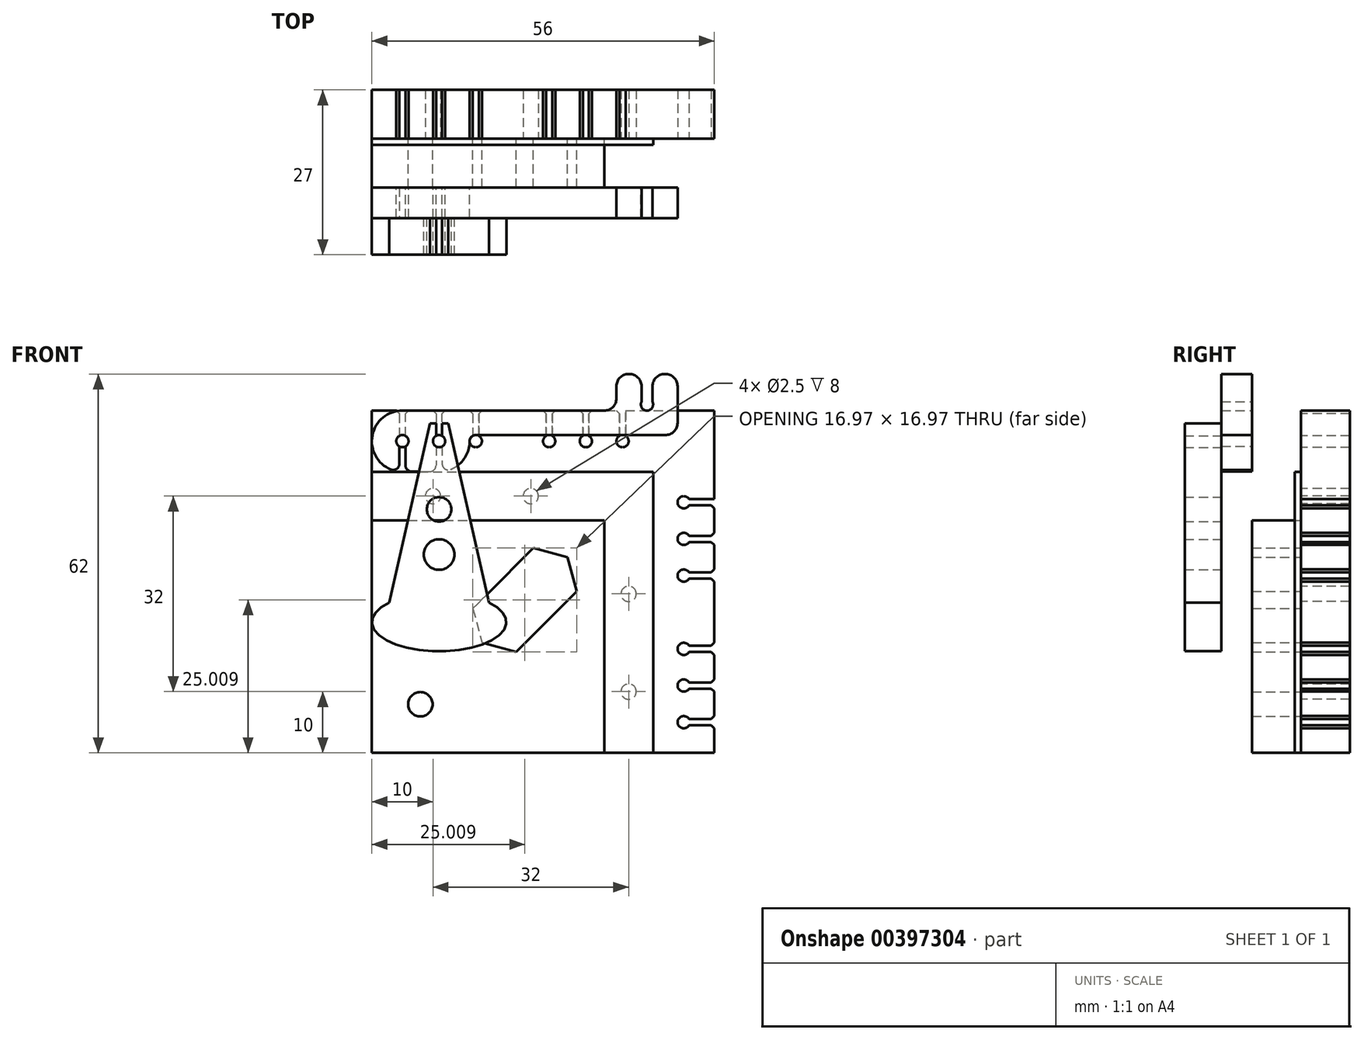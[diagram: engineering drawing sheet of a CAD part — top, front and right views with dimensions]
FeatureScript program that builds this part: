
annotation { "Feature Type Name" : "Feature", "Feature Type Description" : "" }
export const myFeature = defineFeature(function(context is Context, id is Id, definition is map)
    precondition{}
    {
        {
            assignVariable(context, id + "F0", {"name" : "Samm", "anyValue" : 4 * mm});
        }
        {
            assignVariable(context, id + "F1", {"name" : "Auk", "anyValue" : 2 * mm});
        }
        {
            assignVariable(context, id + "F2", {"name" : "Paksus", "anyValue" : getVariable(context, 'Samm') + getVariable(context, 'Auk') + getVariable(context, 'Samm') / 2});
        }
        {
            var Q0;
            Q0=qCreatedBy(makeId("Front.planeOp"),FACE);
            var sketch = newSketch(context, id + "F3", { "sketchPlane" : qUnion([Q0])});
            skLineSegment(sketch, "E0.bottom", {"start": v(0, 0) * mm, "end": v(56, 0) * mm});
            skLineSegment(sketch, "E0.top", {"start": v(0, 56) * mm, "end": v(56, 56) * mm});
            skLineSegment(sketch, "E0.left", {"start": v(0, 0) * mm, "end": v(0, 56) * mm});
            skLineSegment(sketch, "E0.right", {"start": v(56, 0) * mm, "end": v(56, 56) * mm});
            skLineSegment(sketch, "E1", {"start": v(0, 0) * mm, "end": v(56, 56) * mm});
            skLineSegment(sketch, "E2", {"start": v(0, 46) * mm, "end": v(46, 46) * mm});
            skLineSegment(sketch, "E3", {"start": v(0, 38) * mm, "end": v(38, 38) * mm});
            skLineSegment(sketch, "E4", {"start": v(0, 51) * mm, "end": v(56, 51) * mm, "construction": true});
            skLineSegment(sketch, "E5", {"start": v(46, 46) * mm, "end": v(46, 56) * mm, "construction": true});
            skLineSegment(sketch, "E6", {"start": v(38, 38) * mm, "end": v(38, 56) * mm, "construction": true});
            skLineSegment(sketch, "E7", {"start": v(0, 42) * mm, "end": v(42, 42) * mm, "construction": true});
            skPoint(sketch, "E8", {"position": v(26, 42) * mm});
            skPoint(sketch, "E9", {"position": v(10, 42) * mm});
            skSolve(sketch);
        }
        {
            var Q0;
            Q0=qCreatedBy(makeId("Front.planeOp"),FACE);
            var sketch = newSketch(context, id + "F4", { "sketchPlane" : qUnion([Q0])});
            skCircle(sketch, "E10", {"center": v(41, 51) * mm, "radius": 1 * mm});
            skCircle(sketch, "E11", {"center": v(35, 51) * mm, "radius": 1 * mm});
            skLineSegment(sketch, "E12", {"start": v(41.5, 56) * mm, "end": v(41.5, 51.87) * mm});
            skLineSegment(sketch, "E13.MirrorCS", {"start": v(40.5, 56) * mm, "end": v(40.5, 51.87) * mm});
            skLineSegment(sketch, "E14", {"start": v(40.5, 56) * mm, "end": v(41.5, 56) * mm});
            skCircle(sketch, "E15", {"center": v(29, 51) * mm, "radius": 1 * mm});
            skCircle(sketch, "E16", {"center": v(5, 51) * mm, "radius": 1 * mm});
            skLineSegment(sketch, "E17", {"start": v(5.5, 51.87) * mm, "end": v(5.5, 56) * mm});
            skLineSegment(sketch, "E18", {"start": v(5.5, 56) * mm, "end": v(4.5, 56) * mm});
            skLineSegment(sketch, "E19", {"start": v(4.5, 56) * mm, "end": v(4.5, 51.87) * mm});
            skCircle(sketch, "E20", {"center": v(11, 51) * mm, "radius": 1 * mm});
            skLineSegment(sketch, "E21", {"start": v(10.5, 56) * mm, "end": v(10.5, 51.87) * mm});
            skLineSegment(sketch, "E22", {"start": v(10.5, 56) * mm, "end": v(11.5, 56) * mm});
            skLineSegment(sketch, "E23", {"start": v(11.5, 51.87) * mm, "end": v(11.5, 56) * mm});
            skLineSegment(sketch, "E24", {"start": v(29.5, 51.87) * mm, "end": v(29.5, 56) * mm});
            skLineSegment(sketch, "E25", {"start": v(29.5, 56) * mm, "end": v(28.5, 56) * mm});
            skLineSegment(sketch, "E26", {"start": v(28.5, 56) * mm, "end": v(28.5, 51.87) * mm});
            skLineSegment(sketch, "E27", {"start": v(35.5, 51.87) * mm, "end": v(35.5, 56) * mm});
            skLineSegment(sketch, "E28", {"start": v(35.5, 56) * mm, "end": v(34.5, 56) * mm});
            skLineSegment(sketch, "E29", {"start": v(34.5, 56) * mm, "end": v(34.5, 51.87) * mm});
            skCircle(sketch, "E30", {"center": v(17, 51) * mm, "radius": 1 * mm});
            skLineSegment(sketch, "E31", {"start": v(16.5, 56) * mm, "end": v(16.5, 51.87) * mm});
            skLineSegment(sketch, "E32", {"start": v(16.5, 56) * mm, "end": v(17.5, 56) * mm});
            skLineSegment(sketch, "E33", {"start": v(17.5, 51.87) * mm, "end": v(17.5, 56) * mm});
            skSolve(sketch);
        }
        {
            var Q0;
            {var subQ3=sQuery(id+"F3.wireOp",EDGE,"E3");Q0=makeQuery(id+"F3.imprint","IMPRINT",FACE,{"disambiguationData":[TD([[makeQuery(id+"F3.imprint","IMPRINT",EDGE,{"derivedFrom":subQ3}),-1.0]])]});}
            var Q1;
            {var subQ0=sQuery(id+"F3.wireOp",EDGE,"E2");Q1=makeQuery(id+"F3.imprint","IMPRINT",FACE,{"disambiguationData":[TD([[makeQuery(id+"F3.imprint","IMPRINT",EDGE,{"derivedFrom":subQ0}),-1.0]])]});}
            var Q2;
            {var subQ7=sQuery(id+"F3.wireOp",EDGE,"E2");Q2=makeQuery(id+"F3.imprint","IMPRINT",FACE,{"disambiguationData":[TD([[makeQuery(id+"F3.imprint","IMPRINT",EDGE,{"derivedFrom":subQ7}),1.0]])]});}
            extrude(context, id + "F5", {"entities" : qUnion([Q0, Q1, Q2]), "oppositeDirection" : true, "depth" : 8 * mm});
        }
        {
            var Q0;
            {var subQ0=sQuery(id+"F3.wireOp",EDGE,"E2");Q0=makeQuery(id+"F3.imprint","IMPRINT",FACE,{"disambiguationData":[TD([[makeQuery(id+"F3.imprint","IMPRINT",EDGE,{"derivedFrom":subQ0}),-1.0]])]});}
            extrude(context, id + "F6", {"entities" : qUnion([Q0]), "depth" : 1 * mm});
        }
        {
            var Q0;
            {var subQ0=sQuery(id+"F4.wireOp",EDGE,"E16");var subQ1=makeQuery(id+"F4.imprint","INTERSECT",VERTEX,{"derivedFrom":[subQ0,sQuery(id+"F4.wireOp",EDGE,"E17")]});Q0=makeQuery(id+"F4.imprint","IMPRINT",FACE,{"disambiguationData":[TD([[makeQuery(id+"F4.imprint","IMPRINT",EDGE,{"disambiguationData":[TD([[subQ1,-1.0]])],"derivedFrom":subQ0}),1.0]])]});}
            var Q1;
            {var subQ0=sQuery(id+"F4.wireOp",EDGE,"E17");Q1=makeQuery(id+"F4.imprint","IMPRINT",FACE,{"disambiguationData":[TD([[makeQuery(id+"F4.imprint","IMPRINT",EDGE,{"derivedFrom":subQ0}),1.0]])]});}
            var Q2;
            {var subQ0=sQuery(id+"F4.wireOp",EDGE,"E20");var subQ1=makeQuery(id+"F4.imprint","INTERSECT",VERTEX,{"derivedFrom":[subQ0,sQuery(id+"F4.wireOp",EDGE,"E21")]});Q2=makeQuery(id+"F4.imprint","IMPRINT",FACE,{"disambiguationData":[TD([[makeQuery(id+"F4.imprint","IMPRINT",EDGE,{"disambiguationData":[TD([[subQ1,1.0]])],"derivedFrom":subQ0}),1.0]])]});}
            var Q3;
            {var subQ0=sQuery(id+"F4.wireOp",EDGE,"E21");Q3=makeQuery(id+"F4.imprint","IMPRINT",FACE,{"disambiguationData":[TD([[makeQuery(id+"F4.imprint","IMPRINT",EDGE,{"derivedFrom":subQ0}),1.0]])]});}
            var Q4;
            {var subQ0=sQuery(id+"F4.wireOp",EDGE,"QTqNx42c-BT7p-7A9X-RRYs-HgCFCDh2TXWR");Q4=makeQuery(id+"F4.imprint","IMPRINT",FACE,{"disambiguationData":[TD([[makeQuery(id+"F4.imprint","IMPRINT",EDGE,{"derivedFrom":subQ0}),1.0]])]});}
            var Q5;
            {var subQ0=sQuery(id+"F4.wireOp",EDGE,"DebvwMg3-Cwcg-wX2w-ogzT-Ep0VHspPX1UA");var subQ1=makeQuery(id+"F4.imprint","INTERSECT",VERTEX,{"derivedFrom":[subQ0,sQuery(id+"F4.wireOp",EDGE,"NG1M4aDK-SY8a-Geea-gYVj-s5fo7ngXQ215")]});Q5=makeQuery(id+"F4.imprint","IMPRINT",FACE,{"disambiguationData":[TD([[makeQuery(id+"F4.imprint","IMPRINT",EDGE,{"disambiguationData":[TD([[subQ1,-1.0]])],"derivedFrom":subQ0}),1.0]])]});}
            var Q6;
            {var subQ0=sQuery(id+"F4.wireOp",EDGE,"NG1M4aDK-SY8a-Geea-gYVj-s5fo7ngXQ215");Q6=makeQuery(id+"F4.imprint","IMPRINT",FACE,{"disambiguationData":[TD([[makeQuery(id+"F4.imprint","IMPRINT",EDGE,{"derivedFrom":subQ0}),1.0]])]});}
            var Q7;
            {var subQ0=sQuery(id+"F4.wireOp",EDGE,"E15");var subQ1=makeQuery(id+"F4.imprint","INTERSECT",VERTEX,{"derivedFrom":[subQ0,sQuery(id+"F4.wireOp",EDGE,"E24")]});Q7=makeQuery(id+"F4.imprint","IMPRINT",FACE,{"disambiguationData":[TD([[makeQuery(id+"F4.imprint","IMPRINT",EDGE,{"disambiguationData":[TD([[subQ1,-1.0]])],"derivedFrom":subQ0}),1.0]])]});}
            var Q8;
            {var subQ0=sQuery(id+"F4.wireOp",EDGE,"E24");Q8=makeQuery(id+"F4.imprint","IMPRINT",FACE,{"disambiguationData":[TD([[makeQuery(id+"F4.imprint","IMPRINT",EDGE,{"derivedFrom":subQ0}),1.0]])]});}
            var Q9;
            {var subQ0=sQuery(id+"F4.wireOp",EDGE,"E11");var subQ1=makeQuery(id+"F4.imprint","INTERSECT",VERTEX,{"derivedFrom":[subQ0,sQuery(id+"F4.wireOp",EDGE,"E27")]});Q9=makeQuery(id+"F4.imprint","IMPRINT",FACE,{"disambiguationData":[TD([[makeQuery(id+"F4.imprint","IMPRINT",EDGE,{"disambiguationData":[TD([[subQ1,-1.0]])],"derivedFrom":subQ0}),1.0]])]});}
            var Q10;
            {var subQ0=sQuery(id+"F4.wireOp",EDGE,"E27");Q10=makeQuery(id+"F4.imprint","IMPRINT",FACE,{"disambiguationData":[TD([[makeQuery(id+"F4.imprint","IMPRINT",EDGE,{"derivedFrom":subQ0}),1.0]])]});}
            var Q11;
            {var subQ0=sQuery(id+"F4.wireOp",EDGE,"E10");var subQ1=makeQuery(id+"F4.imprint","INTERSECT",VERTEX,{"derivedFrom":[subQ0,sQuery(id+"F4.wireOp",EDGE,"E12")]});Q11=makeQuery(id+"F4.imprint","IMPRINT",FACE,{"disambiguationData":[TD([[makeQuery(id+"F4.imprint","IMPRINT",EDGE,{"disambiguationData":[TD([[subQ1,-1.0]])],"derivedFrom":subQ0}),1.0]])]});}
            var Q12;
            {var subQ0=sQuery(id+"F4.wireOp",EDGE,"E12");Q12=makeQuery(id+"F4.imprint","IMPRINT",FACE,{"disambiguationData":[TD([[makeQuery(id+"F4.imprint","IMPRINT",EDGE,{"derivedFrom":subQ0}),-1.0]])]});}
            var Q13;
            {var subQ0=sQuery(id+"F4.wireOp",EDGE,"e30f7cc4-4558-49b8-8939-138344e96a64");Q13=makeQuery(id+"F4.imprint","IMPRINT",FACE,{"disambiguationData":[TD([[makeQuery(id+"F4.imprint","IMPRINT",EDGE,{"derivedFrom":subQ0}),-1.0]])]});}
            var Q14;
            {var subQ0=sQuery(id+"F4.wireOp",EDGE,"E31");Q14=makeQuery(id+"F4.imprint","IMPRINT",FACE,{"disambiguationData":[TD([[makeQuery(id+"F4.imprint","IMPRINT",EDGE,{"derivedFrom":subQ0}),1.0]])]});}
            var Q15;
            {var subQ0=sQuery(id+"F4.wireOp",EDGE,"E30");var subQ1=makeQuery(id+"F4.imprint","INTERSECT",VERTEX,{"derivedFrom":[subQ0,sQuery(id+"F4.wireOp",EDGE,"E31")]});Q15=makeQuery(id+"F4.imprint","IMPRINT",FACE,{"disambiguationData":[TD([[makeQuery(id+"F4.imprint","IMPRINT",EDGE,{"disambiguationData":[TD([[subQ1,1.0]])],"derivedFrom":subQ0}),1.0]])]});}
            extrude(context, id + "F7", {"entities" : qUnion([Q0, Q1, Q2, Q3, Q4, Q5, Q6, Q7, Q8, Q9, Q10, Q11, Q12, Q13, Q14, Q15]), "operationType" : NewBodyOperationType.REMOVE, "endBound" : BoundingType.UP_TO_NEXT, "oppositeDirection" : true, "depth" : 25 * mm});
        }
        {
            var Q0;
            Q0=makeQuery(id+"F7.boolean.opBoolean","COPY",EDGE,{"derivedFrom":makeQuery(id+"F7.opExtrude","SWEPT_EDGE",EDGE,{"disambiguationData":[OSD([sQuery(id+"F4.wireOp",EDGE,"E18"),sQuery(id+"F4.wireOp",EDGE,"E19")])]})});
            var Q1;
            Q1=makeQuery(id+"F7.boolean.opBoolean","COPY",EDGE,{"derivedFrom":makeQuery(id+"F7.opExtrude","SWEPT_EDGE",EDGE,{"disambiguationData":[OSD([sQuery(id+"F4.wireOp",EDGE,"E17"),sQuery(id+"F4.wireOp",EDGE,"E18")])]})});
            var Q2;
            Q2=makeQuery(id+"F7.boolean.opBoolean","COPY",EDGE,{"derivedFrom":makeQuery(id+"F7.opExtrude","SWEPT_EDGE",EDGE,{"disambiguationData":[OSD([sQuery(id+"F4.wireOp",EDGE,"E21"),sQuery(id+"F4.wireOp",EDGE,"E22")])]})});
            var Q3;
            Q3=makeQuery(id+"F7.boolean.opBoolean","COPY",EDGE,{"derivedFrom":makeQuery(id+"F7.opExtrude","SWEPT_EDGE",EDGE,{"disambiguationData":[OSD([sQuery(id+"F4.wireOp",EDGE,"E22"),sQuery(id+"F4.wireOp",EDGE,"E23")])]})});
            var Q4;
            Q4=makeQuery(id+"F7.boolean.opBoolean","COPY",EDGE,{"derivedFrom":makeQuery(id+"F7.opExtrude","SWEPT_EDGE",EDGE,{"disambiguationData":[OSD([sQuery(id+"F4.wireOp",EDGE,"E13.MirrorCS"),sQuery(id+"F4.wireOp",EDGE,"E14")])]})});
            var Q5;
            Q5=makeQuery(id+"F7.boolean.opBoolean","COPY",EDGE,{"derivedFrom":makeQuery(id+"F7.opExtrude","SWEPT_EDGE",EDGE,{"disambiguationData":[OSD([sQuery(id+"F4.wireOp",EDGE,"E12"),sQuery(id+"F4.wireOp",EDGE,"E14")])]})});
            var Q6;
            Q6=makeQuery(id+"F7.boolean.opBoolean","COPY",EDGE,{"derivedFrom":makeQuery(id+"F7.opExtrude","SWEPT_EDGE",EDGE,{"disambiguationData":[OSD([sQuery(id+"F4.wireOp",EDGE,"E27"),sQuery(id+"F4.wireOp",EDGE,"E28")])]})});
            var Q7;
            Q7=makeQuery(id+"F7.boolean.opBoolean","COPY",EDGE,{"derivedFrom":makeQuery(id+"F7.opExtrude","SWEPT_EDGE",EDGE,{"disambiguationData":[OSD([sQuery(id+"F4.wireOp",EDGE,"E28"),sQuery(id+"F4.wireOp",EDGE,"E29")])]})});
            var Q8;
            Q8=makeQuery(id+"F7.boolean.opBoolean","COPY",EDGE,{"derivedFrom":makeQuery(id+"F7.opExtrude","SWEPT_EDGE",EDGE,{"disambiguationData":[OSD([sQuery(id+"F4.wireOp",EDGE,"E24"),sQuery(id+"F4.wireOp",EDGE,"E25")])]})});
            var Q9;
            Q9=makeQuery(id+"F7.boolean.opBoolean","COPY",EDGE,{"derivedFrom":makeQuery(id+"F7.opExtrude","SWEPT_EDGE",EDGE,{"disambiguationData":[OSD([sQuery(id+"F4.wireOp",EDGE,"E25"),sQuery(id+"F4.wireOp",EDGE,"E26")])]})});
            var Q10;
            Q10=makeQuery(id+"F7.boolean.opBoolean","COPY",EDGE,{"derivedFrom":makeQuery(id+"F7.opExtrude","SWEPT_EDGE",EDGE,{"disambiguationData":[OSD([sQuery(id+"F4.wireOp",EDGE,"E31"),sQuery(id+"F4.wireOp",EDGE,"E32")])]})});
            var Q11;
            Q11=makeQuery(id+"F7.boolean.opBoolean","COPY",EDGE,{"derivedFrom":makeQuery(id+"F7.opExtrude","SWEPT_EDGE",EDGE,{"disambiguationData":[OSD([sQuery(id+"F4.wireOp",EDGE,"E32"),sQuery(id+"F4.wireOp",EDGE,"E33")])]})});
            chamfer(context, id + "F8", {"entities" : qUnion([Q0, Q1, Q2, Q3, Q4, Q5, Q6, Q7, Q8, Q9, Q10, Q11]), "width" : 0.5 * mm, "tangentPropagation" : true});
        }
        {
            var Q0;
            Q0=sQuery(id+"F3.wireOp",VERTEX,"E9");
            var Q1;
            Q1=sQuery(id+"F3.wireOp",VERTEX,"E8");
            var Q2;
            Q2=makeQuery(id+"F5.opExtrude","SWEPT_BODY",BODY,{"disambiguationData":[OSD([sQuery(id+"F3.wireOp",EDGE,"E0.top"),sQuery(id+"F3.wireOp",EDGE,"E0.left"),sQuery(id+"F3.wireOp",EDGE,"E1")])]});
            hole(context, id + "F9", {"style" : HoleStyle.SIMPLE, "endStyle" : HoleEndStyle.THROUGH, "holeDiameter" : 2.5 * mm, "isTappedThrough" : true, "tappedDepth" : 12 * mm, "tapClearance" : 3, "locations" : qUnion([Q0, Q1]), "scope" : qUnion([Q2])});
        }
        {
            var Q0;
            Q0=makeQuery(id+"F5.opExtrude","SWEPT_BODY",BODY,{"disambiguationData":[OSD([sQuery(id+"F3.wireOp",EDGE,"E0.top"),sQuery(id+"F3.wireOp",EDGE,"E0.left"),sQuery(id+"F3.wireOp",EDGE,"E1")])]});
            var Q1;
            Q1=makeQuery(id+"F5.opExtrude","SWEPT_FACE",FACE,{"disambiguationData":[OSD([sQuery(id+"F3.wireOp",EDGE,"E1")])]});
            mirror(context, id + "F10", {"operationType" : NewBodyOperationType.ADD, "entities" : qUnion([Q0]), "mirrorPlane" : qUnion([Q1])});
        }
        {
            var Q0;
            Q0=makeQuery(id+"F6.opExtrude","SWEPT_BODY",BODY,{"disambiguationData":[OSD([sQuery(id+"F3.wireOp",EDGE,"E0.left"),sQuery(id+"F3.wireOp",EDGE,"E1"),sQuery(id+"F3.wireOp",EDGE,"E2"),sQuery(id+"F3.wireOp",EDGE,"E3")])]});
            var Q1;
            Q1=makeQuery(id+"F6.opExtrude","SWEPT_FACE",FACE,{"disambiguationData":[OSD([sQuery(id+"F3.wireOp",EDGE,"E1")])]});
            mirror(context, id + "F11", {"operationType" : NewBodyOperationType.ADD, "entities" : qUnion([Q0]), "mirrorPlane" : qUnion([Q1])});
        }
        {
            var Q0;
            {var subQ3=sQuery(id+"F3.wireOp",EDGE,"E3");Q0=makeQuery(id+"F3.imprint","IMPRINT",FACE,{"disambiguationData":[TD([[makeQuery(id+"F3.imprint","IMPRINT",EDGE,{"derivedFrom":subQ3}),-1.0]])]});}
            var sketch = newSketch(context, id + "F12", { "sketchPlane" : qUnion([Q0])});
            skLineSegment(sketch, "E34.0", {"start": v(0, 38) * mm, "end": v(38, 38) * mm});
            skLineSegment(sketch, "E35.0", {"start": v(38, 0) * mm, "end": v(38, 38) * mm});
            skLineSegment(sketch, "E36.0", {"start": v(0, 0) * mm, "end": v(0, 56) * mm});
            skLineSegment(sketch, "E37.0", {"start": v(0, 0) * mm, "end": v(56, 0) * mm});
            skLineSegment(sketch, "E38.0", {"start": v(0, 0) * mm, "end": v(56, 56) * mm});
            skLineSegment(sketch, "E39", {"start": v(32, 32) * mm, "end": v(26.42, 33.5) * mm});
            skLineSegment(sketch, "E40", {"start": v(26.42, 33.5) * mm, "end": v(16.52, 23.6) * mm});
            skLineSegment(sketch, "E41", {"start": v(16.52, 23.6) * mm, "end": v(18.02, 18.02) * mm});
            skLineSegment(sketch, "E42.MirrorCS", {"start": v(23.6, 16.52) * mm, "end": v(18.02, 18.02) * mm});
            skLineSegment(sketch, "E43.MirrorCS", {"start": v(32, 32) * mm, "end": v(33.5, 26.42) * mm});
            skLineSegment(sketch, "E44.MirrorCS", {"start": v(33.5, 26.42) * mm, "end": v(23.6, 16.52) * mm});
            skPoint(sketch, "E45", {"position": v(7.93, 7.93) * mm});
            skSolve(sketch);
        }
        {
            var Q0;
            Q0=qSketchRegion(id+"F12",true);
            extrude(context, id + "F13", {"entities" : qUnion([Q0]), "depth" : getVariable(context, 'Paksus')});
        }
        {
            var Q0;
            Q0=makeQuery(id+"F13.opExtrude","CAP_FACE",FACE,{"disambiguationData":[OSD([sQuery(id+"F12.wireOp",EDGE,"E34.0"),sQuery(id+"F12.wireOp",EDGE,"E35.0"),sQuery(id+"F12.wireOp",EDGE,"E36.0"),sQuery(id+"F12.wireOp",EDGE,"E37.0"),sQuery(id+"F12.wireOp",EDGE,"2cf8d3c9-5500-4004-992a-a7f99b6d44c5.0"),sQuery(id+"F12.wireOp",EDGE,"2cf8d3c9-5500-4004-992a-a7f99b6d44c5.1"),sQuery(id+"F12.wireOp",EDGE,"2cf8d3c9-5500-4004-992a-a7f99b6d44c5.2"),sQuery(id+"F12.wireOp",EDGE,"2cf8d3c9-5500-4004-992a-a7f99b6d44c5.3"),sQuery(id+"F12.wireOp",EDGE,"2cf8d3c9-5500-4004-992a-a7f99b6d44c5.4"),sQuery(id+"F12.wireOp",EDGE,"2cf8d3c9-5500-4004-992a-a7f99b6d44c5.5")])],"isStart":false});
            var sketch = newSketch(context, id + "F14", { "sketchPlane" : qUnion([Q0])});
            skCircle(sketch, "E46.0", {"center": v(5, 51) * mm, "radius": 1 * mm});
            skCircle(sketch, "E47.0", {"center": v(11, 51) * mm, "radius": 1 * mm});
            skCircle(sketch, "E48.0", {"center": v(41, 51) * mm, "radius": 1 * mm});
            skCircle(sketch, "E49", {"center": v(11, 51) * mm, "radius": 5 * mm});
            skCircle(sketch, "E50", {"center": v(5, 51) * mm, "radius": 5 * mm});
            skLineSegment(sketch, "E51.0", {"start": v(0, 51) * mm, "end": v(56, 51) * mm, "construction": true});
            skCircle(sketch, "E52", {"center": v(45, 57) * mm, "radius": 1 * mm});
            skLineSegment(sketch, "E53", {"start": v(50, 52) * mm, "end": v(15.9, 52) * mm});
            skLineSegment(sketch, "E54", {"start": v(4.5, 50.13) * mm, "end": v(4.5, 46.03) * mm});
            skLineSegment(sketch, "E55", {"start": v(5.5, 50.13) * mm, "end": v(5.5, 46.03) * mm});
            skLineSegment(sketch, "E56", {"start": v(10.5, 50.13) * mm, "end": v(10.5, 46.03) * mm});
            skLineSegment(sketch, "E57", {"start": v(11.5, 50.13) * mm, "end": v(11.5, 46.03) * mm});
            skLineSegment(sketch, "E58", {"start": v(5.5, 46.03) * mm, "end": v(10.5, 46.03) * mm});
            skLineSegment(sketch, "E59.0", {"start": v(46, 46) * mm, "end": v(46, 56) * mm, "construction": true});
            skLineSegment(sketch, "E60", {"start": v(45.9, 57.44) * mm, "end": v(45.9, 62) * mm});
            skLineSegment(sketch, "E61", {"start": v(44.1, 57.44) * mm, "end": v(44.1, 62) * mm});
            skLineSegment(sketch, "E62", {"start": v(50, 52) * mm, "end": v(50, 62) * mm});
            skLineSegment(sketch, "E63", {"start": v(50, 62) * mm, "end": v(40, 62) * mm});
            skLineSegment(sketch, "E64", {"start": v(40, 62) * mm, "end": v(40, 56) * mm});
            skLineSegment(sketch, "E65", {"start": v(40, 56) * mm, "end": v(5, 56) * mm});
            skPoint(sketch, "E66.orphan", {"position": v(0, 62) * mm});
            skPoint(sketch, "E67.start.orphan", {"position": v(0, 56) * mm});
            skSolve(sketch);
        }
        {
            var Q0;
            {var subQ0=sQuery(id+"F14.wireOp",EDGE,"E56");Q0=makeQuery(id+"F14.imprint","IMPRINT",FACE,{"disambiguationData":[TD([[makeQuery(id+"F14.imprint","IMPRINT",EDGE,{"derivedFrom":subQ0}),-1.0]])]});}
            var Q1;
            {var subQ0=sQuery(id+"F14.wireOp",EDGE,"AxJx2oVJ-XFwZ-MC76-LPeR-xshG9jsGcbUg");var subQ1=sQuery(id+"F14.wireOp",EDGE,"E49");var subQ2=makeQuery(id+"F14.imprint","INTERSECT",VERTEX,{"derivedFrom":[subQ1,subQ0]});Q1=makeQuery(id+"F14.imprint","IMPRINT",FACE,{"disambiguationData":[TD([[makeQuery(id+"F14.imprint","IMPRINT",EDGE,{"disambiguationData":[TD([[subQ2,-1.0]])],"derivedFrom":subQ1}),-1.0]])]});}
            var Q2;
            {var subQ0=sQuery(id+"F14.wireOp",EDGE,"E58");Q2=makeQuery(id+"F14.imprint","IMPRINT",FACE,{"disambiguationData":[TD([[makeQuery(id+"F14.imprint","IMPRINT",EDGE,{"derivedFrom":subQ0}),1.0]])]});}
            var Q3;
            {var subQ0=sQuery(id+"F14.wireOp",EDGE,"CSsFTJs7-Jaks-gvLE-uZ3l-TUTck8eSOqBI");Q3=makeQuery(id+"F14.imprint","IMPRINT",FACE,{"disambiguationData":[TD([[makeQuery(id+"F14.imprint","IMPRINT",EDGE,{"derivedFrom":subQ0}),-1.0]])]});}
            var Q4;
            {var subQ2=sQuery(id+"F14.wireOp",EDGE,"E54");Q4=makeQuery(id+"F14.imprint","IMPRINT",FACE,{"disambiguationData":[TD([[makeQuery(id+"F14.imprint","IMPRINT",EDGE,{"derivedFrom":subQ2}),-1.0]])]});}
            var Q5;
            {var subQ2=sQuery(id+"F14.wireOp",EDGE,"E57");Q5=makeQuery(id+"F14.imprint","IMPRINT",FACE,{"disambiguationData":[TD([[makeQuery(id+"F14.imprint","IMPRINT",EDGE,{"derivedFrom":subQ2}),1.0]])]});}
            var Q6;
            {var subQ6=sQuery(id+"F14.wireOp",EDGE,"E60");var subQ8=sQuery(id+"F14.wireOp",EDGE,"E52");var subQ9=makeQuery(id+"F14.imprint","INTERSECT",VERTEX,{"derivedFrom":[subQ8,subQ6]});Q6=makeQuery(id+"F14.imprint","IMPRINT",FACE,{"disambiguationData":[TD([[makeQuery(id+"F14.imprint","IMPRINT",EDGE,{"disambiguationData":[TD([[subQ9,1.0]])],"derivedFrom":subQ8}),-1.0]])]});}
            var Q7;
            {var subQ0=sQuery(id+"F14.wireOp",EDGE,"E55");Q7=makeQuery(id+"F14.imprint","IMPRINT",FACE,{"disambiguationData":[TD([[makeQuery(id+"F14.imprint","IMPRINT",EDGE,{"derivedFrom":subQ0}),1.0]])]});}
            var Q8;
            {var subQ0=sQuery(id+"F14.wireOp",EDGE,"E55");Q8=makeQuery(id+"F14.imprint","IMPRINT",FACE,{"disambiguationData":[TD([[makeQuery(id+"F14.imprint","IMPRINT",EDGE,{"derivedFrom":subQ0}),1.0]])]});}
            var Q9;
            {var subQ0=sQuery(id+"F14.wireOp",EDGE,"E56");Q9=makeQuery(id+"F14.imprint","IMPRINT",FACE,{"disambiguationData":[TD([[makeQuery(id+"F14.imprint","IMPRINT",EDGE,{"derivedFrom":subQ0}),-1.0]])]});}
            var Q10;
            {var subQ0=sQuery(id+"F14.wireOp",EDGE,"E53");var subQ1=sQuery(id+"F14.wireOp",EDGE,"E49");var subQ2=makeQuery(id+"F14.imprint","INTERSECT",VERTEX,{"derivedFrom":[subQ1,subQ0]});Q10=makeQuery(id+"F14.imprint","IMPRINT",FACE,{"disambiguationData":[TD([[makeQuery(id+"F14.imprint","IMPRINT",EDGE,{"disambiguationData":[TD([[subQ2,-1.0]])],"derivedFrom":subQ1}),-1.0]])]});}
            var Q11;
            {var subQ0=sQuery(id+"F14.wireOp",EDGE,"E49");var subQ1=makeQuery(id+"F14.imprint","INTERSECT",VERTEX,{"derivedFrom":[sQuery(id+"F14.wireOp",EDGE,"E46.0"),subQ0]});Q11=makeQuery(id+"F14.imprint","IMPRINT",FACE,{"disambiguationData":[TD([[makeQuery(id+"F14.imprint","IMPRINT",EDGE,{"disambiguationData":[TD([[subQ1,1.0]])],"derivedFrom":subQ0}),1.0]])]});}
            var Q12;
            {var subQ0=sQuery(id+"F14.wireOp",EDGE,"E49");var subQ1=makeQuery(id+"F14.imprint","INTERSECT",VERTEX,{"derivedFrom":[sQuery(id+"F14.wireOp",EDGE,"E46.0"),subQ0]});Q12=makeQuery(id+"F14.imprint","IMPRINT",FACE,{"disambiguationData":[TD([[makeQuery(id+"F14.imprint","IMPRINT",EDGE,{"disambiguationData":[TD([[subQ1,1.0]])],"derivedFrom":subQ0}),1.0]])]});}
            var Q13;
            {var subQ2=sQuery(id+"F14.wireOp",EDGE,"E54");Q13=makeQuery(id+"F14.imprint","IMPRINT",FACE,{"disambiguationData":[TD([[makeQuery(id+"F14.imprint","IMPRINT",EDGE,{"derivedFrom":subQ2}),-1.0]])]});}
            var Q14;
            {var subQ0=sQuery(id+"F14.wireOp",EDGE,"BxTuXfEc-kO9Q-QHb8-LTs3-kqM6wV0efrVW");var subQ1=sQuery(id+"F14.wireOp",EDGE,"E48.0");var subQ2=makeQuery(id+"F14.imprint","INTERSECT",VERTEX,{"derivedFrom":[subQ1,subQ0]});Q14=makeQuery(id+"F14.imprint","IMPRINT",FACE,{"disambiguationData":[TD([[makeQuery(id+"F14.imprint","IMPRINT",EDGE,{"disambiguationData":[TD([[subQ2,-1.0]])],"derivedFrom":subQ1}),-1.0]])]});}
            extrude(context, id + "F15", {"entities" : qUnion([Q0, Q1, Q2, Q3, Q4, Q5, Q6, Q7, Q8, Q9, Q10, Q11, Q12, Q13, Q14]), "depth" : 5 * mm});
        }
        {
            var Q0;
            Q0=makeQuery(id+"F15.opExtrude","SWEPT_EDGE",EDGE,{"disambiguationData":[OSD([sQuery(id+"F14.wireOp",EDGE,"E50"),sQuery(id+"F14.wireOp",EDGE,"E54")])]});
            var Q1;
            Q1=makeQuery(id+"F15.opExtrude","SWEPT_EDGE",EDGE,{"disambiguationData":[OSD([sQuery(id+"F14.wireOp",EDGE,"E50"),sQuery(id+"F14.wireOp",EDGE,"E55"),sQuery(id+"F14.wireOp",EDGE,"E58")])]});
            var Q2;
            Q2=makeQuery(id+"F15.opExtrude","SWEPT_EDGE",EDGE,{"disambiguationData":[OSD([sQuery(id+"F14.wireOp",EDGE,"E49"),sQuery(id+"F14.wireOp",EDGE,"E56"),sQuery(id+"F14.wireOp",EDGE,"E58")])]});
            var Q3;
            Q3=makeQuery(id+"F15.opExtrude","SWEPT_EDGE",EDGE,{"disambiguationData":[OSD([sQuery(id+"F14.wireOp",EDGE,"E49"),sQuery(id+"F14.wireOp",EDGE,"E57")])]});
            var Q4;
            Q4=makeQuery(id+"F15.opExtrude","SWEPT_EDGE",EDGE,{"disambiguationData":[OSD([sQuery(id+"F14.wireOp",EDGE,"AxJx2oVJ-XFwZ-MC76-LPeR-xshG9jsGcbUg"),sQuery(id+"F14.wireOp",EDGE,"ckgy3OCV-uk7f-uJ41-MpvO-jaV0Tc8mXzn0")])]});
            var Q5;
            Q5=makeQuery(id+"F15.opExtrude","SWEPT_EDGE",EDGE,{"disambiguationData":[OSD([sQuery(id+"F14.wireOp",EDGE,"AxJx2oVJ-XFwZ-MC76-LPeR-xshG9jsGcbUg"),sQuery(id+"F14.wireOp",EDGE,"Tde4fxld-xR9Y-IW79-mpMQ-LUkHlr8zzJhR")])]});
            var Q6;
            Q6=makeQuery(id+"F15.opExtrude","SWEPT_EDGE",EDGE,{"disambiguationData":[OSD([sQuery(id+"F14.wireOp",EDGE,"E49"),sQuery(id+"F14.wireOp",EDGE,"E53")])]});
            fillet(context, id + "F16", {"entities" : qUnion([Q0, Q1, Q2, Q3, Q4, Q5, Q6]), "radius" : 1 * mm, "tangentPropagation" : true, "allowEdgeOverflow" : false});
        }
        {
            var Q0;
            Q0=sQuery(id+"F12.wireOp",VERTEX,"E45");
            var Q1;
            Q1=makeQuery(id+"F13.opExtrude","SWEPT_BODY",BODY,{"disambiguationData":[OSD([sQuery(id+"F12.wireOp",EDGE,"E34.0"),sQuery(id+"F12.wireOp",EDGE,"E35.0"),sQuery(id+"F12.wireOp",EDGE,"E36.0"),sQuery(id+"F12.wireOp",EDGE,"E37.0"),sQuery(id+"F12.wireOp",EDGE,"E39"),sQuery(id+"F12.wireOp",EDGE,"E40"),sQuery(id+"F12.wireOp",EDGE,"E41"),sQuery(id+"F12.wireOp",EDGE,"E42.MirrorCS"),sQuery(id+"F12.wireOp",EDGE,"E44.MirrorCS"),sQuery(id+"F12.wireOp",EDGE,"E43.MirrorCS")])]});
            hole(context, id + "F17", {"style" : HoleStyle.SIMPLE, "endStyle" : HoleEndStyle.THROUGH, "oppositeDirection" : true, "holeDiameter" : 4 * mm, "isTappedThrough" : true, "tappedDepth" : 12 * mm, "tapClearance" : 3, "locations" : qUnion([Q0]), "scope" : qUnion([Q1])});
        }
        {
            var Q0;
            Q0=makeQuery(id+"F15.opExtrude","SWEPT_EDGE",EDGE,{"disambiguationData":[OSD([sQuery(id+"F14.wireOp",EDGE,"E64"),sQuery(id+"F14.wireOp",EDGE,"E65")])]});
            var Q1;
            Q1=makeQuery(id+"F15.opExtrude","SWEPT_EDGE",EDGE,{"disambiguationData":[OSD([sQuery(id+"F14.wireOp",EDGE,"E63"),sQuery(id+"F14.wireOp",EDGE,"E64")])]});
            var Q2;
            Q2=makeQuery(id+"F15.opExtrude","SWEPT_EDGE",EDGE,{"disambiguationData":[OSD([sQuery(id+"F14.wireOp",EDGE,"E61"),sQuery(id+"F14.wireOp",EDGE,"E63")])]});
            var Q3;
            Q3=makeQuery(id+"F15.opExtrude","SWEPT_EDGE",EDGE,{"disambiguationData":[OSD([sQuery(id+"F14.wireOp",EDGE,"E60"),sQuery(id+"F14.wireOp",EDGE,"E63")])]});
            var Q4;
            Q4=makeQuery(id+"F15.opExtrude","SWEPT_EDGE",EDGE,{"disambiguationData":[OSD([sQuery(id+"F14.wireOp",EDGE,"E62"),sQuery(id+"F14.wireOp",EDGE,"E63")])]});
            var Q5;
            Q5=makeQuery(id+"F15.opExtrude","SWEPT_EDGE",EDGE,{"disambiguationData":[OSD([sQuery(id+"F14.wireOp",EDGE,"E53"),sQuery(id+"F14.wireOp",EDGE,"E62")])]});
            fillet(context, id + "F18", {"entities" : qUnion([Q0, Q1, Q2, Q3, Q4, Q5]), "radius" : 2 * mm, "tangentPropagation" : true, "allowEdgeOverflow" : false});
        }
        {
            var Q0;
            Q0=makeQuery(id+"F15.opExtrude","CAP_FACE",FACE,{"disambiguationData":[OSD([sQuery(id+"F14.wireOp",EDGE,"E46.0"),sQuery(id+"F14.wireOp",EDGE,"E47.0"),sQuery(id+"F14.wireOp",EDGE,"E49"),sQuery(id+"F14.wireOp",EDGE,"E50"),sQuery(id+"F14.wireOp",EDGE,"E52"),sQuery(id+"F14.wireOp",EDGE,"E53"),sQuery(id+"F14.wireOp",EDGE,"E54"),sQuery(id+"F14.wireOp",EDGE,"E55"),sQuery(id+"F14.wireOp",EDGE,"E56"),sQuery(id+"F14.wireOp",EDGE,"E57"),sQuery(id+"F14.wireOp",EDGE,"E58"),sQuery(id+"F14.wireOp",EDGE,"E60"),sQuery(id+"F14.wireOp",EDGE,"E61"),sQuery(id+"F14.wireOp",EDGE,"E62"),sQuery(id+"F14.wireOp",EDGE,"E63"),sQuery(id+"F14.wireOp",EDGE,"E64"),sQuery(id+"F14.wireOp",EDGE,"E65")])],"isStart":false});
            var sketch = newSketch(context, id + "F19", { "sketchPlane" : qUnion([Q0])});
            skLineSegment(sketch, "E68.0", {"start": v(10.5, 56) * mm, "end": v(10.5, 51.87) * mm});
            skLineSegment(sketch, "E69.0", {"start": v(11.5, 51.87) * mm, "end": v(11.5, 56) * mm});
            skCircle(sketch, "E70.0", {"center": v(11, 51) * mm, "radius": 1 * mm});
            skLineSegment(sketch, "E71", {"start": v(10.5, 53.93) * mm, "end": v(9.5, 53.93) * mm});
            skLineSegment(sketch, "E72", {"start": v(12.5, 53.93) * mm, "end": v(11.5, 53.93) * mm});
            skEllipse(sketch, "E73", {"center": v(11, 21.37) * mm, "majorRadius": 11 * mm, "minorRadius": 4.75 * mm, "majorAxis": v(-1, 0)});
            skLineSegment(sketch, "E74", {"start": v(9.5, 53.93) * mm, "end": v(2.83, 24.55) * mm});
            skLineSegment(sketch, "E75", {"start": v(12.5, 53.93) * mm, "end": v(19.17, 24.55) * mm});
            skCircle(sketch, "E76", {"center": v(11, 39.84) * mm, "radius": 2 * mm});
            skCircle(sketch, "E77", {"center": v(11, 32.44) * mm, "radius": 2.5 * mm});
            skSolve(sketch);
        }
        {
            var Q0;
            {var subQ1=sQuery(id+"F19.wireOp",EDGE,"E71");Q0=makeQuery(id+"F19.imprint","IMPRINT",FACE,{"disambiguationData":[TD([[makeQuery(id+"F19.imprint","IMPRINT",EDGE,{"derivedFrom":subQ1}),1.0]])]});}
            var Q1;
            {var subQ1=sQuery(id+"F19.wireOp",EDGE,"E72");Q1=makeQuery(id+"F19.imprint","IMPRINT",FACE,{"disambiguationData":[TD([[makeQuery(id+"F19.imprint","IMPRINT",EDGE,{"derivedFrom":subQ1}),1.0]])]});}
            var Q2;
            {var subQ11=sQuery(id+"F14.wireOp",EDGE,"E56");var subQ12=makeQuery(id+"F15.opExtrude","CAP_EDGE",EDGE,{"disambiguationData":[OSD([subQ11])],"isStart":false});Q2=makeQuery(id+"F19.imprint","IMPRINT",FACE,{"disambiguationData":[TD([[makeQuery(id+"F19.imprint","IMPRINT",EDGE,{"derivedFrom":subQ12}),1.0]])]});}
            var Q3;
            {var subQ0=sQuery(id+"F19.wireOp",EDGE,"E73");var subQ1=makeQuery(id+"F19.imprint","INTERSECT",VERTEX,{"derivedFrom":[subQ0,sQuery(id+"F19.wireOp",EDGE,"E74")]});Q3=makeQuery(id+"F19.imprint","IMPRINT",FACE,{"disambiguationData":[TD([[makeQuery(id+"F19.imprint","IMPRINT",EDGE,{"disambiguationData":[TD([[subQ1,1.0]])],"derivedFrom":subQ0}),1.0]])]});}
            extrude(context, id + "F20", {"entities" : qUnion([Q0, Q1, Q2, Q3]), "depth" : 6 * mm});
        }
    });
